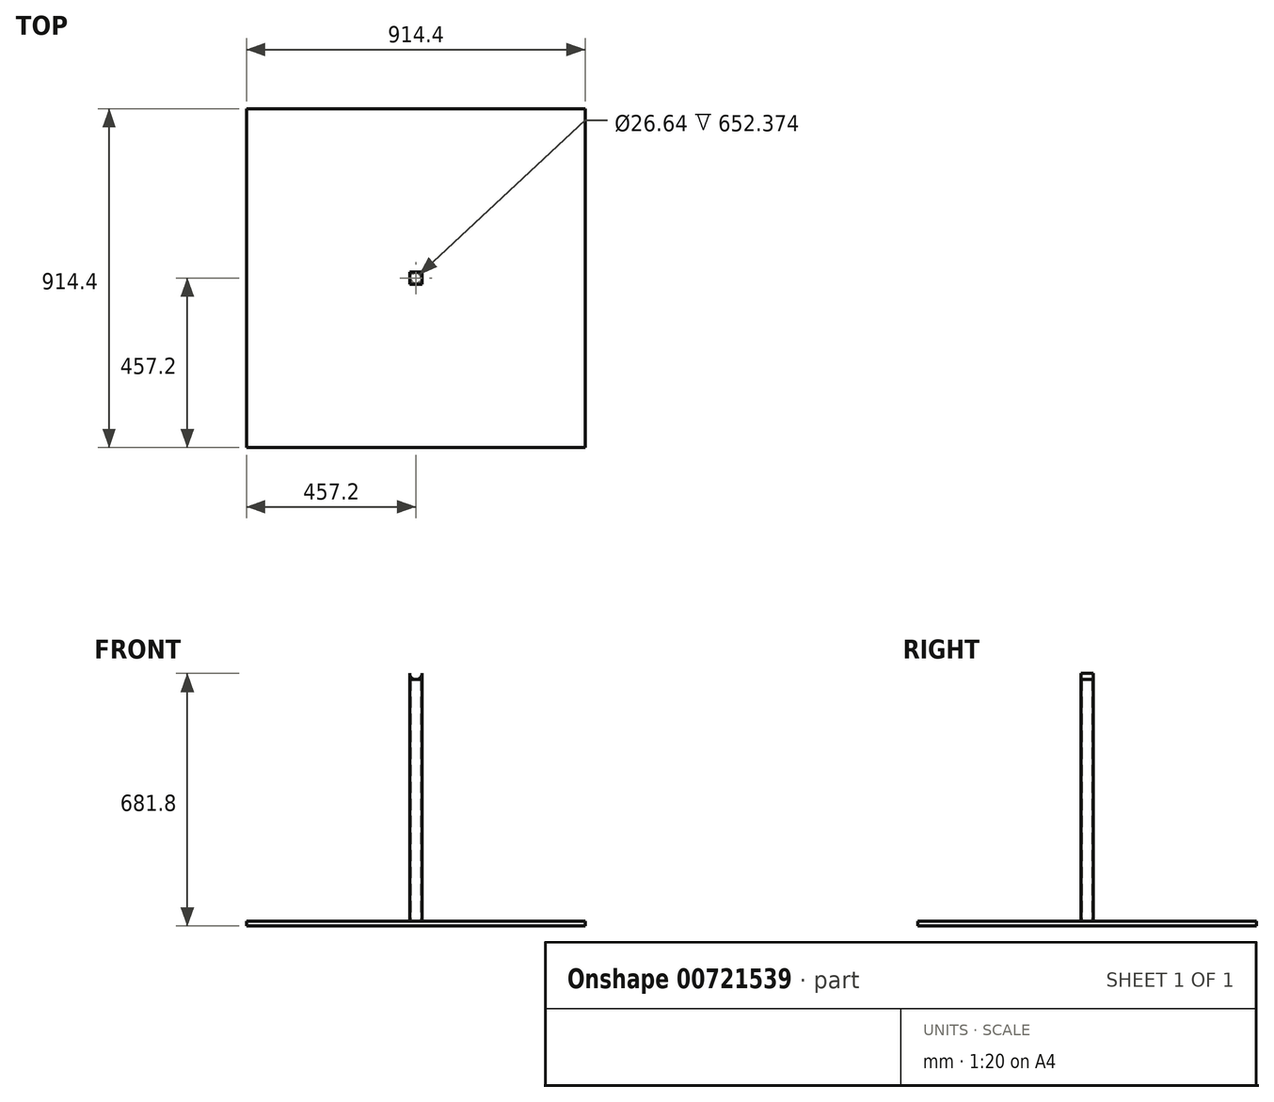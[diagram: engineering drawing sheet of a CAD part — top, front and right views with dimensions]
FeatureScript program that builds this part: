
annotation { "Feature Type Name" : "Feature", "Feature Type Description" : "" }
export const myFeature = defineFeature(function(context is Context, id is Id, definition is map)
    precondition{}
    {
        {
            var Q0;
            Q0=qCreatedBy(makeId("Top.planeOp"),FACE);
            var sketch = newSketch(context, id + "F0", { "sketchPlane" : qUnion([Q0])});
            skLineSegment(sketch, "E0.bottom", {"start": v(457.2, 457.2) * mm, "end": v(-457.2, 457.2) * mm});
            skLineSegment(sketch, "E0.top", {"start": v(457.2, -457.2) * mm, "end": v(-457.2, -457.2) * mm});
            skLineSegment(sketch, "E0.left", {"start": v(457.2, 457.2) * mm, "end": v(457.2, -457.2) * mm});
            skLineSegment(sketch, "E0.right", {"start": v(-457.2, 457.2) * mm, "end": v(-457.2, -457.2) * mm});
            skPoint(sketch, "E0.middle", {"position": v(0, 0) * mm});
            skSolve(sketch);
        }
        {
            var Q0;
            Q0 = qSketchRegion(id + "F0", true);
            extrude(context, id + "F1", {"entities" : qUnion([Q0]), "oppositeDirection" : true, "depth" : 12.7 * mm, "offsetDistance" : 25.4 * mm});
        }
        {
            var Q0;
            Q0=makeQuery(id+"F1.opExtrude","CAP_FACE",FACE,{"disambiguationData":[OSD([sQuery(id+"F0.wireOp",EDGE,"E0.bottom"),sQuery(id+"F0.wireOp",EDGE,"E0.top"),sQuery(id+"F0.wireOp",EDGE,"E0.left"),sQuery(id+"F0.wireOp",EDGE,"E0.right")])],"isStart":true});
            var sketch = newSketch(context, id + "F2", { "sketchPlane" : qUnion([Q0])});
            skCircle(sketch, "E1", {"center": v(-440.5, 440.5) * mm, "radius": 16.7 * mm});
            skCircle(sketch, "E2", {"center": v(-440.5, 440.5) * mm, "radius": 13.32 * mm});
            skCircle(sketch, "E3", {"center": v(0, 440.5) * mm, "radius": 16.7 * mm});
            skCircle(sketch, "E4", {"center": v(0, 440.5) * mm, "radius": 13.32 * mm});
            skCircle(sketch, "E5", {"center": v(-440.5, 0) * mm, "radius": 16.7 * mm});
            skCircle(sketch, "E6", {"center": v(-440.5, 0) * mm, "radius": 13.32 * mm});
            skPoint(sketch, "E7.MirrorP", {"position": v(440.5, 440.5) * mm});
            skCircle(sketch, "E8.MirrorC", {"center": v(440.5, 440.5) * mm, "radius": 16.7 * mm});
            skCircle(sketch, "E9.MirrorC", {"center": v(440.5, 440.5) * mm, "radius": 13.32 * mm});
            skCircle(sketch, "E10.MirrorC", {"center": v(440.5, 0) * mm, "radius": 13.32 * mm});
            skCircle(sketch, "E11.MirrorC", {"center": v(440.5, 0) * mm, "radius": 16.7 * mm});
            skCircle(sketch, "E12.MirrorC", {"center": v(440.5, -440.5) * mm, "radius": 13.32 * mm});
            skCircle(sketch, "E13.MirrorC", {"center": v(0, -440.5) * mm, "radius": 13.32 * mm});
            skCircle(sketch, "E14.MirrorC", {"center": v(-440.5, -440.5) * mm, "radius": 13.32 * mm});
            skCircle(sketch, "E15.MirrorC", {"center": v(0, -440.5) * mm, "radius": 16.7 * mm});
            skCircle(sketch, "E16.MirrorC", {"center": v(440.5, -440.5) * mm, "radius": 16.7 * mm});
            skCircle(sketch, "E17.MirrorC", {"center": v(-440.5, -440.5) * mm, "radius": 16.7 * mm});
            skSolve(sketch);
        }
        {
            var Q0;
            {var subQ0=sQuery(id+"F2.wireOp",EDGE,"E3");Q0=makeQuery(id+"F2.imprint","IMPRINT",FACE,{"disambiguationData":[TD([[makeQuery(id+"F2.imprint","IMPRINT",EDGE,{"derivedFrom":subQ0}),-1.0]])]});}
            var sketch = newSketch(context, id + "F3", { "sketchPlane" : qUnion([Q0])});
            skCircle(sketch, "E18", {"center": v(0, 0) * mm, "radius": 16.7 * mm});
            skCircle(sketch, "E19", {"center": v(0, 0) * mm, "radius": 13.32 * mm});
            skSolve(sketch);
        }
        {
            var Q0;
            Q0 = qSketchRegion(id + "F3", true);
            extrude(context, id + "F4", {"entities" : qUnion([Q0]), "depth" : 685.8 * mm, "offsetDistance" : 25.4 * mm});
        }
        {
            var Q0;
            Q0=makeQuery(id+"F4.opExtrude","CAP_FACE",FACE,{"disambiguationData":[OSD([sQuery(id+"F3.wireOp",EDGE,"E18"),sQuery(id+"F3.wireOp",EDGE,"E19")])],"isStart":false});
            var sketch = newSketch(context, id + "F5", { "sketchPlane" : qUnion([Q0])});
            skLineSegment(sketch, "E20.bottom", {"start": v(16.7, 16.7) * mm, "end": v(-16.7, 16.7) * mm});
            skLineSegment(sketch, "E20.top", {"start": v(16.7, -16.7) * mm, "end": v(-16.7, -16.7) * mm});
            skLineSegment(sketch, "E20.left", {"start": v(16.7, 16.7) * mm, "end": v(16.7, -16.7) * mm});
            skLineSegment(sketch, "E20.right", {"start": v(-16.7, 16.7) * mm, "end": v(-16.7, -16.7) * mm});
            skPoint(sketch, "E20.middle", {"position": v(0, 0) * mm});
            skSolve(sketch);
        }
        {
            var Q0;
            Q0 = qSketchRegion(id + "F5", true);
            extrude(context, id + "F6", {"entities" : qUnion([Q0]), "operationType" : NewBodyOperationType.ADD, "oppositeDirection" : true, "depth" : 33.43 * mm, "offsetDistance" : 25.4 * mm});
        }
        {
            var Q0;
            Q0=makeQuery(id+"F6.opExtrude","SWEPT_FACE",FACE,{"disambiguationData":[OSD([sQuery(id+"F5.wireOp",EDGE,"E20.top")])]});
            var sketch = newSketch(context, id + "F7", { "sketchPlane" : qUnion([Q0])});
            skCircle(sketch, "E21", {"center": v(0, 669.1) * mm, "radius": 16.7 * mm});
            skSolve(sketch);
        }
        {
            var Q0;
            Q0 = qSketchRegion(id + "F7", true);
            extrude(context, id + "F8", {"entities" : qUnion([Q0]), "operationType" : NewBodyOperationType.REMOVE, "oppositeDirection" : true, "depth" : 33.4 * mm, "offsetDistance" : 25.4 * mm});
        }
        {
            var Q0;
            {var subQ0=sQuery(id+"F5.wireOp",EDGE,"E20.right");var subQ1=sQuery(id+"F5.wireOp",EDGE,"E20.top");Q0=makeQuery(id+"F8.boolean.opBoolean","SPLIT",FACE,{"disambiguationData":[TD([makeQuery(id+"F4.opExtrude","CAP_FACE",FACE,{"disambiguationData":[OSD([sQuery(id+"F3.wireOp",EDGE,"E18"),sQuery(id+"F3.wireOp",EDGE,"E19")])],"isStart":false}),makeQuery(id+"F6.opExtrude","CAP_FACE",FACE,{"disambiguationData":[OSD([sQuery(id+"F5.wireOp",EDGE,"E20.bottom"),subQ1,sQuery(id+"F5.wireOp",EDGE,"E20.left"),subQ0])],"isStart":true}),makeQuery(id+"F6.opExtrude","SWEPT_FACE",FACE,{"disambiguationData":[OSD([subQ0])]}),makeQuery(id+"F8.opExtrude","SWEPT_FACE",FACE,{"disambiguationData":[OSD([sQuery(id+"F7.wireOp",EDGE,"E21")])]})])],"derivedFrom":makeQuery(id+"F6.opExtrude","SWEPT_FACE",FACE,{"disambiguationData":[OSD([subQ1])]})});}
            var sketch = newSketch(context, id + "F9", { "sketchPlane" : qUnion([Q0])});
            skCircle(sketch, "E22", {"center": v(0, 669.1) * mm, "radius": 16.7 * mm});
            skLineSegment(sketch, "E23", {"start": v(0, 685.8) * mm, "end": v(-16.7, 685.8) * mm});
            skLineSegment(sketch, "E24", {"start": v(-16.7, 685.8) * mm, "end": v(-16.7, 669.1) * mm});
            skSolve(sketch);
        }
        {
            var Q0;
            Q0 = qSketchRegion(id + "F9", true);
            extrude(context, id + "F10", {"entities" : qUnion([Q0]), "operationType" : NewBodyOperationType.REMOVE, "oppositeDirection" : true, "depth" : 33.4 * mm, "offsetDistance" : 25.4 * mm});
        }
        {
            var Q0;
            {var subQ0=sQuery(id+"F5.wireOp",EDGE,"E20.left");var subQ1=sQuery(id+"F5.wireOp",EDGE,"E20.top");Q0=makeQuery(id+"F8.boolean.opBoolean","SPLIT",FACE,{"disambiguationData":[TD([makeQuery(id+"F4.opExtrude","CAP_FACE",FACE,{"disambiguationData":[OSD([sQuery(id+"F3.wireOp",EDGE,"E18"),sQuery(id+"F3.wireOp",EDGE,"E19")])],"isStart":false}),makeQuery(id+"F6.opExtrude","CAP_FACE",FACE,{"disambiguationData":[OSD([sQuery(id+"F5.wireOp",EDGE,"E20.bottom"),subQ1,subQ0,sQuery(id+"F5.wireOp",EDGE,"E20.right")])],"isStart":true}),makeQuery(id+"F6.opExtrude","SWEPT_FACE",FACE,{"disambiguationData":[OSD([subQ0])]}),makeQuery(id+"F8.opExtrude","SWEPT_FACE",FACE,{"disambiguationData":[OSD([sQuery(id+"F7.wireOp",EDGE,"E21")])]})])],"derivedFrom":makeQuery(id+"F6.opExtrude","SWEPT_FACE",FACE,{"disambiguationData":[OSD([subQ1])]})});}
            var sketch = newSketch(context, id + "F11", { "sketchPlane" : qUnion([Q0])});
            skCircle(sketch, "E25", {"center": v(0, 669.1) * mm, "radius": 16.7 * mm});
            skLineSegment(sketch, "E26", {"start": v(0, 685.8) * mm, "end": v(16.7, 685.8) * mm});
            skLineSegment(sketch, "E27", {"start": v(16.7, 685.8) * mm, "end": v(16.7, 669.1) * mm});
            skSolve(sketch);
        }
        {
            var Q0;
            Q0 = qSketchRegion(id + "F11", true);
            extrude(context, id + "F12", {"entities" : qUnion([Q0]), "operationType" : NewBodyOperationType.REMOVE, "oppositeDirection" : true, "depth" : 33.4 * mm, "offsetDistance" : 25.4 * mm});
        }
    });
